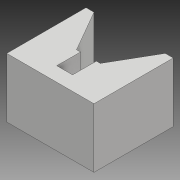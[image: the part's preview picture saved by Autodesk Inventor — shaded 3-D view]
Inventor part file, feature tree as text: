
AUTODESK INVENTOR PART (.ipt)
format: ipt  version: 2018 (Build 220112000, 112)  size: 133,120 bytes
history: native  units: mm
features: extrude x4, sketch x3, other x1
ambient origin geometry x8: Origin, YZ Plane, XZ Plane, XY Plane, X Axis, Y Axis, Z Axis, Center Point
bodies: Body1 (feature_tree), Body2 (feature_tree)
feature tree (8):
  other  "Sólido1"
  extrude  "Extrusión1"  Depth=2.0mm
  extrude  "Extrusión2"  TaperAngle=60.0deg  [1 undecoded]
  sketch  "Boceto3"  dims[d4=5.0mm d5=6.0mm d6=12.0mm d7=2.0mm d8=15.0mm d9=0.0mm d10=1.0mm d11=6.0mm d12=4.0mm d13=12.0mm d14=0.0mm d16=1.5mm d23=1.5mm d24=1.5mm d25=1.5mm d26=3.0mm d27=4.0mm d29=1.0mm d30=3.0mm d31=0.0mm d32=1.0mm d33=0.0mm]
  extrude  "Extrusión3"  Depth=6.0mm
  extrude  "Extrusión4"  Depth=12.0mm
  sketch  "Boceto1"  dims[d0=15.0mm d1=2.0mm]
  sketch  "Boceto2"  dims[d2=12.0mm d3=60.0deg]
note: 1 required parameter value undecoded (feature->parameter linkage not recoverable at this tier; creation-order binding heuristic only, values carry confidence <= 0.55)
